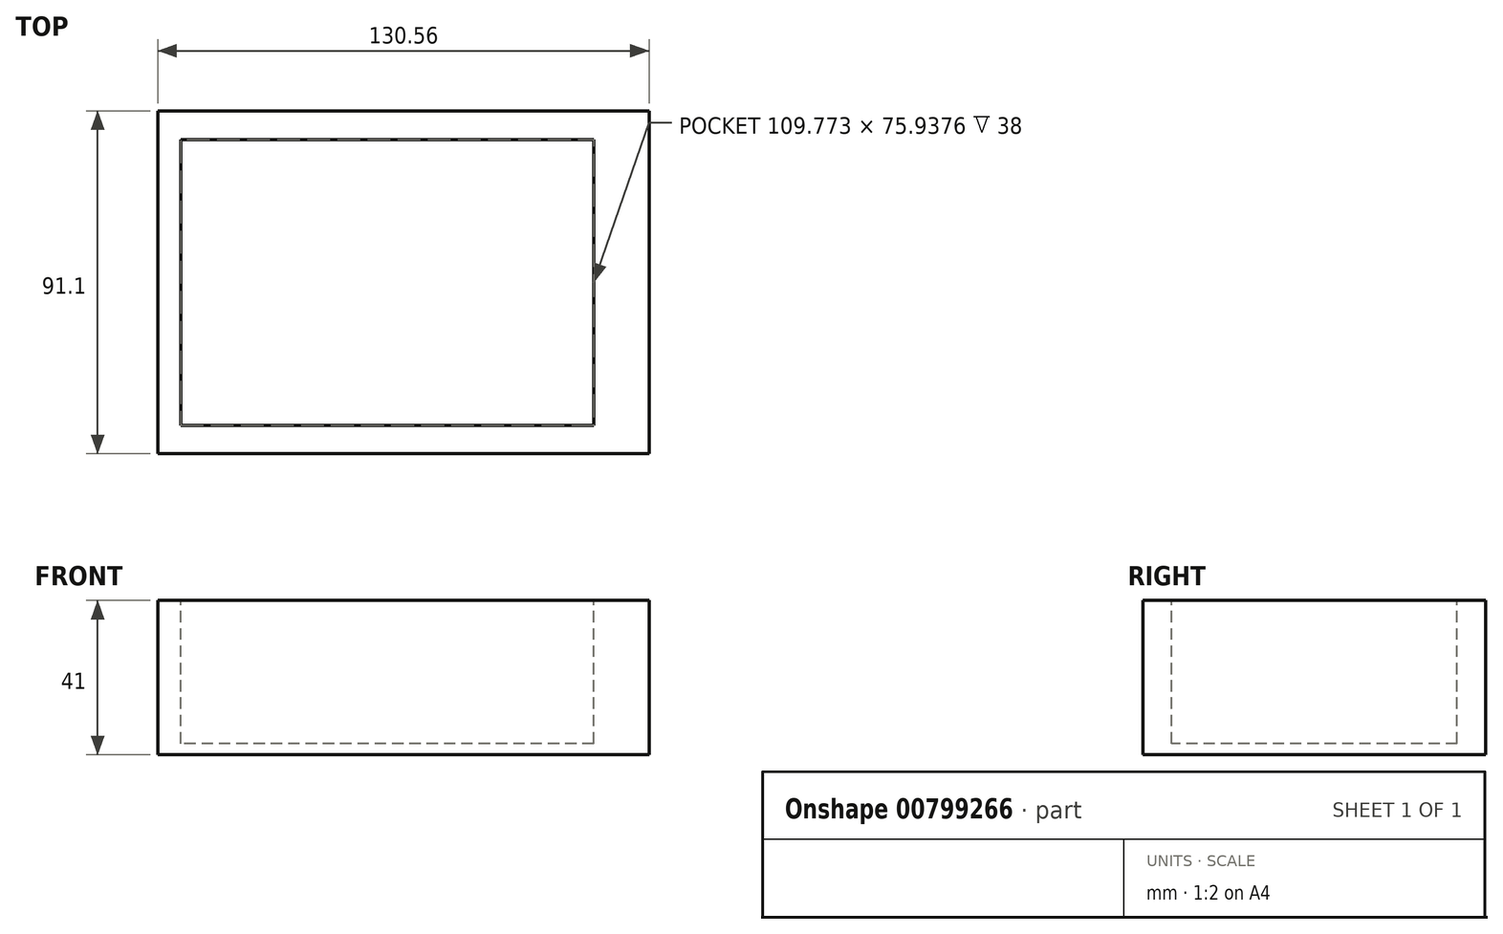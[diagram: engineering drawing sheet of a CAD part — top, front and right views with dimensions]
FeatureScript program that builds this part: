
annotation { "Feature Type Name" : "Feature", "Feature Type Description" : "" }
export const myFeature = defineFeature(function(context is Context, id is Id, definition is map)
    precondition{}
    {
        {
            var Q0;
            Q0=qCreatedBy(makeId("Top.planeOp"),FACE);
            var sketch = newSketch(context, id + "F0", { "sketchPlane" : qUnion([Q0])});
            skLineSegment(sketch, "E0.bottom", {"start": v(-65.28, 45.55) * mm, "end": v(65.28, 45.55) * mm});
            skLineSegment(sketch, "E0.top", {"start": v(-65.28, -45.55) * mm, "end": v(65.28, -45.55) * mm});
            skLineSegment(sketch, "E0.left", {"start": v(-65.28, 45.55) * mm, "end": v(-65.28, -45.55) * mm});
            skLineSegment(sketch, "E0.right", {"start": v(65.28, 45.55) * mm, "end": v(65.28, -45.55) * mm});
            skPoint(sketch, "E0.middle", {"position": v(0, 0) * mm});
            skSolve(sketch);
        }
        {
            var Q0;
            Q0 = qSketchRegion(id + "F0", true);
            extrude(context, id + "F1", {"entities" : qUnion([Q0]), "depth" : 41 * mm, "offsetDistance" : 25 * mm});
        }
        {
            var Q0;
            Q0=makeQuery(id+"F1.opExtrude","CAP_FACE",FACE,{"disambiguationData":[OSD([sQuery(id+"F0.wireOp",EDGE,"E0.bottom"),sQuery(id+"F0.wireOp",EDGE,"E0.top"),sQuery(id+"F0.wireOp",EDGE,"E0.left"),sQuery(id+"F0.wireOp",EDGE,"E0.right")])],"isStart":false});
            var sketch = newSketch(context, id + "F2", { "sketchPlane" : qUnion([Q0])});
            skPoint(sketch, "E1.middle", {"position": v(-4.3, 0) * mm});
            skLineSegment(sketch, "E2.bottom", {"start": v(50.58, 37.97) * mm, "end": v(-59.2, 37.97) * mm});
            skLineSegment(sketch, "E2.top", {"start": v(50.58, -37.97) * mm, "end": v(-59.2, -37.97) * mm});
            skLineSegment(sketch, "E2.left", {"start": v(50.58, 37.97) * mm, "end": v(50.58, -37.97) * mm});
            skLineSegment(sketch, "E2.right", {"start": v(-59.2, 37.97) * mm, "end": v(-59.2, -37.97) * mm});
            skSolve(sketch);
        }
        {
            var Q0;
            Q0=makeQuery(id+"F2.imprint","IMPRINT",FACE,{"disambiguationData":[TD([[makeQuery(id+"F2.imprint","IMPRINT",EDGE,{"derivedFrom":sQuery(id+"F2.wireOp",EDGE,"E2.bottom")}),1.0]])]});
            extrude(context, id + "F3", {"entities" : qUnion([Q0]), "operationType" : NewBodyOperationType.REMOVE, "oppositeDirection" : true, "depth" : 38 * mm, "offsetDistance" : 25 * mm});
        }
    });
